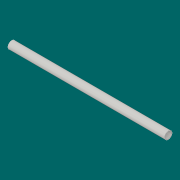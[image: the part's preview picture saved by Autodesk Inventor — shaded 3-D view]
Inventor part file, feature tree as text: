
AUTODESK INVENTOR PART (.ipt)
format: ipt  version: 2016 (Build 200138000, 138)  size: 70,656 bytes
history: native  units: mm
features: extrude x1, sketch x1
ambient origin geometry x8: Origin, YZ Plane, XZ Plane, XY Plane, X Axis, Y Axis, Z Axis, Center Point
bodies: Solid1 (feature_tree)
feature tree (2):
  extrude  "Extrusion1"  Depth=1219.2mm
  sketch  "Sketch1"  dims[d0=60.325mm d1=51.9938mm d2=1219.2mm d3=0.0mm]
